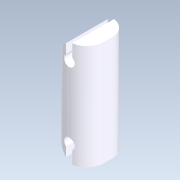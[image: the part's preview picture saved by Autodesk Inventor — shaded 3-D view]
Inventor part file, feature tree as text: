
AUTODESK INVENTOR PART (.ipt)
format: ipt  version: 2020.2 (Build 242310000, 310)  size: 157,184 bytes
history: native  units: mm
features: extrude x3, sketch x3, fillet x1
ambient origin geometry x8: Origin, YZ Plane, XZ Plane, XY Plane, X Axis, Y Axis, Z Axis, Center Point
bodies: Solid1 (feature_tree)
feature tree (7):
  extrude  "Extrusion1"  Depth=50.0mm
  extrude  "Extrusion2"  Depth=17.0mm
  fillet  "Fillet1"  Radius=17.0mm
  extrude  "Extrusion4"  TaperAngle=0.0deg  [1 undecoded]
  sketch  "Sketch1"  dims[d1=2.5mm d2=50.0mm]
  sketch  "Sketch2"  dims[d3=5.0mm d5=17.0mm d9=17.0mm]
  sketch  "Sketch4"  dims[d10=2.5mm d11=0.0mm d12=135.0deg d13=135.0deg d14=20.0mm d15=0.0mm d16=8.0mm d17=5.0mm d18=1.5mm d19=3.0mm d20=8.0mm d21=1.5mm d22=1.5mm d23=5.0mm d24=0.0mm d25=0.0mm d26=8.0mm d31=2.0mm d32=2.0mm d33=0.0mm d34=0.0mm]
note: 1 required parameter value undecoded (feature->parameter linkage not recoverable at this tier; creation-order binding heuristic only, values carry confidence <= 0.55)
